FCSTD DOCUMENT  (FreeCAD 0.18R4 (GitTag))
Label: tmp
License: All rights reserved
LicenseURL: http://en.wikipedia.org/wiki/All_rights_reserved
objects: Sketcher::SketchObject×6, PartDesign::Body×2, Spreadsheet::Sheet×1
note: 8 computed .brp shape members not serialized (recipe doc carries the construction recipe); baked Part::Feature solids carry a one-line shape summary decoded from their .brp

FEATURE [Spreadsheet::Sheet] Spreadsheet  label="Variables"
  cells = A2=slotNumber; B2(slotNumber)=12; A3=outerDiameter; B3(outerDiameter)=32; A4=innerDiameter; B4(innerDiameter)=6; A5=stackLength; B5(stackLength)=31; A6=stackingFactor; B6(stackingFactor)=0.95; A7=cuttingThickness; B7(cuttingThickness)=0.1; A8=skewAngle; B8(skewAngle)=14.5; A9=segmentAngle; B9(segmentAngle)==360 / slotNumber; A10=tipHeightReduction; B10(tipHeightReduction)=0; A11=toothThickness; B11(toothThickness)=2.2; A12=yokeThickness; B12(yokeThickness)=5; A13=tipHeight; B13(tipHeight)=1.5; A14=tipAngle; B14(tipAngle)=90; A15=openingLeft; B15(openingLeft)=1; A16=openingRight; B16(openingRight)=1; A17=slotIsolation; B17(slotIsolation)=0.25; A18=windingAngle; B18(windingAngle)=35; A19=heightRatio; B19(heightRatio)=40; A20=roundingRadii; B20(roundingRadii)=0.3; A21=coilAxialHeight; B21(coilAxialHeight)=7.896000000000001
FEATURE [Sketcher::SketchObject] Sketch003  label="StatorSegment"
  MapMode = 5
  Support = -> [XY_Plane]
  expr: Constraints[71] = Variables.innerDiameter / 2
  expr: Constraints[26] = Variables.toothThickness / 2
  expr: Constraints[9] = Variables.segmentAngle
  expr: Constraints[27] = Variables.innerDiameter / 2 + Variables.yokeThickness
  expr: Constraints[35] = Variables.roundingRadii
  expr: Constraints[61] = Variables.tipHeight
  expr: Constraints[23] = Variables.tipAngle
  expr: Constraints[16] = Variables.tipHeight * (1 - Variables.tipHeightReduction / 100)
  expr: Constraints[12] = Variables.openingLeft
  expr: Constraints[72] = Variables.segmentAngle / 2
  expr: Constraints[5] = Variables.outerDiameter
  sketch-geometry (29):
    g0: ArcOfCircle [constr] CenterX=0 CenterY=0 CenterZ=0 NormalX=0 NormalY=0 NormalZ=1 AngleXU=0 Radius=16 StartAngle=0 EndAngle=0.523599
    g1: LineSegment [constr] StartX=0 StartY=0 StartZ=0 EndX=13.8564 EndY=8 EndZ=0
    g2: LineSegment [constr] StartX=0 StartY=0 StartZ=0 EndX=16 EndY=3e-16 EndZ=0
    g3: LineSegment [constr] StartX=0 StartY=0 StartZ=0 EndX=15.4548 EndY=4.1411 EndZ=0
    g4: LineSegment [constr] StartX=11.9984 StartY=10.5848 StartZ=0 EndX=15.1659 EndY=5.09847 EndZ=0
    g5: LineSegment [constr] StartX=15.1659 StartY=5.09847 StartZ=0 EndX=13.9394 EndY=4.76982 EndZ=0
    g6: LineSegment [constr] StartX=13.717 StartY=4.71024 StartZ=0 EndX=15.1659 EndY=5.09847 EndZ=0
    g7: ArcOfCircle CenterX=4.32e-14 CenterY=2.49e-14 CenterZ=0 NormalX=0 NormalY=0 NormalZ=1 AngleXU=0 Radius=16 StartAngle=0.32431 EndAngle=0.523599
    g8: LineSegment StartX=13.6019 StartY=4.9096 StartZ=0 EndX=13.0274 EndY=5.90478 EndZ=0
    g9: LineSegment StartX=12.6176 StartY=6.01459 StartZ=0 EndX=7.66671 EndY=3.1562 EndZ=0
    g10: LineSegment StartX=7.52693 StartY=2.81875 StartZ=0 EndX=7.72741 EndY=2.07055 EndZ=0
    g11: LineSegment [constr] StartX=7.66671 StartY=3.1562 StartZ=0 EndX=7.11671 EndY=4.10883 EndZ=0
    g12: LineSegment StartX=7.72741 StartY=2.07055 StartZ=0 EndX=7.92789 EndY=1.32235 EndZ=0
    g13: LineSegment StartX=8.21766 StartY=1.1 StartZ=0 EndX=13.9344 EndY=1.1 EndZ=0
    g14: LineSegment StartX=14.2344 StartY=1.4 StartZ=0 EndX=14.2344 EndY=2.54914 EndZ=0
    g15: LineSegment StartX=14.4568 StartY=2.83891 StartZ=0 EndX=15.6833 EndY=3.16756 EndZ=0
    g16: ArcOfCircle CenterX=6.7e-15 CenterY=0 CenterZ=0 NormalX=0 NormalY=0 NormalZ=1 AngleXU=0 Radius=16 StartAngle=0 EndAngle=0.199289
    g17: ArcOfCircle CenterX=14.5344 CenterY=2.54914 CenterZ=0 NormalX=0 NormalY=0 NormalZ=1 AngleXU=0 Radius=0.3 StartAngle=1.8326 EndAngle=3.14159
    g18: ArcOfCircle CenterX=13.9344 CenterY=1.4 CenterZ=0 NormalX=0 NormalY=0 NormalZ=1 AngleXU=0 Radius=0.3 StartAngle=4.71239 EndAngle=6.28319
    g19: ArcOfCircle CenterX=8.21766 CenterY=1.4 CenterZ=0 NormalX=0 NormalY=0 NormalZ=1 AngleXU=0 Radius=0.3 StartAngle=3.40339 EndAngle=4.71239
    g20: ArcOfCircle CenterX=12.7676 CenterY=5.75478 CenterZ=0 NormalX=0 NormalY=0 NormalZ=1 AngleXU=0 Radius=0.3 StartAngle=0.523599 EndAngle=2.0944
    g21: ArcOfCircle CenterX=13.8618 CenterY=5.0596 CenterZ=0 NormalX=0 NormalY=0 NormalZ=1 AngleXU=0 Radius=0.3 StartAngle=3.66519 EndAngle=4.97419
    g22: ArcOfCircle CenterX=7.81671 CenterY=2.8964 CenterZ=0 NormalX=0 NormalY=0 NormalZ=1 AngleXU=0 Radius=0.3 StartAngle=2.0944 EndAngle=3.40339
    g23: LineSegment [constr] StartX=13.6019 StartY=4.9096 StartZ=0 EndX=13.717 EndY=4.71024 EndZ=0
    g24: LineSegment [constr] StartX=13.717 StartY=4.71024 StartZ=0 EndX=13.9394 EndY=4.76982 EndZ=0
    g25: LineSegment StartX=13.9394 StartY=4.76982 StartZ=0 EndX=15.1659 EndY=5.09847 EndZ=0
    g26: LineSegment StartX=13.8564 StartY=8 StartZ=0 EndX=2.59808 EndY=1.5 EndZ=0
    g27: LineSegment StartX=3 StartY=1e-16 StartZ=0 EndX=16 EndY=3e-16 EndZ=0
    g28: ArcOfCircle CenterX=0 CenterY=0 CenterZ=0 NormalX=0 NormalY=0 NormalZ=1 AngleXU=0 Radius=3 StartAngle=0 EndAngle=0.523599
  constraints (73):
    c: Coincident(g0,g-1)
    c: Coincident(g1,g0)
    c: Coincident(g1,g0)
    c: Coincident(g2,g0)
    c: Coincident(g2,g0)
    c: Diameter(g0) = 32
    c: Coincident(g3,g0)
    c: PointOnObject(g3,g0)
    c: Symmetric(g0,g0,g3)
    c: Angle(g2,g1) = 0.523599
    c: PointOnObject(g4,g0)
    c: Symmetric(g4,g4,g1)
    c: Distance(g4,g3) = 1
    c: Coincident(g5,g4)
    c: Parallel(g5,g3)
    c: PointOnObject(g6,g5)
    c: Distance(g6) = 1.5
    c: Coincident(g7,g0)
    c: Coincident(g7,g6)
    c: PointOnObject(g7,g1)
    c: PointOnObject(g10,g3)
    c: Perpendicular(g3,g10)
    c: Parallel(g1,g9)
    c: Angle(g9,g8) = 1.5708
    c: PointOnObject(g11,g1)
    c: Perpendicular(g1,g11)
    c: Distance(g11) = 1.1
    c: Distance(g-1,g10) = 8
    c: Coincident(g12,g10)
    c: Symmetric(g15,g7,g3)
    c: PointOnObject(g16,g2)
    c: Coincident(g16,g0)
    c: Coincident(g16,g15)
    c: Tangent(g14,g17) = 1.5708
    c: Tangent(g15,g17) = 1.5708
    c: Radius(g17) = 0.3
    c: Tangent(g13,g18) = -1.5708
    c: Tangent(g14,g18) = -1.5708
    c: Tangent(g12,g19) = -1.5708
    c: Tangent(g13,g19) = -1.5708
    c: Tangent(g8,g20) = -1.5708
    c: Tangent(g9,g20) = -1.5708
    c: Tangent(g5,g21) = 1.5708
    c: Tangent(g8,g21) = 1.5708
    c: Tangent(g10,g22) = -1.5708
    c: Tangent(g9,g22) = -1.5708
    c: Coincident(g11,g9)
    c: Equal(g17,g18)
    c: Equal(g19,g17)
    c: Equal(g22,g17)
    c: Equal(g20,g17)
    c: Symmetric(g13,g9,g3)
    c: Symmetric(g14,g8,g3)
    c: Symmetric(g14,g8,g3)
    c: Equal(g21,g17)
    c: Coincident(g23,g8)
    c: Coincident(g24,g23)
    c: Coincident(g24,g5)
    c: Parallel(g23,g8)
    c: Parallel(g24,g5)
    c: Coincident(g6,g23)
    c: Distance(g6,g4) = 1.5
    c: Coincident(g25,g21)
    c: Coincident(g25,g7)
    c: Coincident(g26,g7)
    c: PointOnObject(g26,g1)
    c: PointOnObject(g27,g2)
    c: Coincident(g27,g16)
    c: Coincident(g28,g-1)
    c: Coincident(g28,g26)
    c: Coincident(g28,g27)
    c: Radius(g28) = 3
    c: Angle(g-1,g3) = 0.261799
FEATURE [Sketcher::SketchObject] Sketch  label="StatorSde"
  MapMode = 5
  Support = -> [XY_Plane001]
  expr: Constraints[20] = Variables.stackLength
  expr: Constraints[17] = Variables.innerDiameter
  expr: Constraints[16] = Variables.outerDiameter
  sketch-geometry (8):
    g0: LineSegment StartX=-15.5 StartY=16 StartZ=0 EndX=15.5 EndY=16 EndZ=0
    g1: LineSegment StartX=15.5 StartY=16 StartZ=0 EndX=15.5 EndY=3 EndZ=0
    g2: LineSegment StartX=15.5 StartY=3 StartZ=0 EndX=-15.5 EndY=3 EndZ=0
    g3: LineSegment StartX=-15.5 StartY=3 StartZ=0 EndX=-15.5 EndY=16 EndZ=0
    g4: LineSegment StartX=-15.5 StartY=-3 StartZ=0 EndX=15.5 EndY=-3 EndZ=0
    g5: LineSegment StartX=15.5 StartY=-3 StartZ=0 EndX=15.5 EndY=-16 EndZ=0
    g6: LineSegment StartX=15.5 StartY=-16 StartZ=0 EndX=-15.5 EndY=-16 EndZ=0
    g7: LineSegment StartX=-15.5 StartY=-16 StartZ=0 EndX=-15.5 EndY=-3 EndZ=0
  constraints (21):
    c: Coincident(g0,g1)
    c: Coincident(g1,g2)
    c: Coincident(g2,g3)
    c: Coincident(g3,g0)
    c: Horizontal(g0)
    c: Vertical(g1)
    c: Vertical(g3)
    c: Coincident(g4,g5)
    c: Coincident(g5,g6)
    c: Coincident(g6,g7)
    c: Coincident(g7,g4)
    c: Horizontal(g6)
    c: Vertical(g5)
    c: Vertical(g7)
    c: Symmetric(g2,g1,g-2)
    c: Symmetric(g4,g4,g-2)
    c: DistanceY(g6,g0) = 32
    c: DistanceY(g4,g2) = 6
    c: Symmetric(g4,g2,g-1)
    c: Equal(g7,g3)
    c: DistanceX(g6,g6) = 31
FEATURE [Sketcher::SketchObject] Sketch009  label="WindingSide"
  ExternalGeometry = -> [Sketch]
  MapMode = 5
  Support = -> [XY_Plane001]
  expr: Constraints[18] = Variables.coilAxialHeight
  expr: Constraints[8] = Variables.coilAxialHeight
  sketch-geometry (12):
    g0: ArcOfEllipse CenterX=-15.5 CenterY=0 CenterZ=0 NormalX=0 NormalY=0 NormalZ=1 MajorRadius=16 MinorRadius=7.896 AngleXU=1.5708 StartAngle=0 EndAngle=3.14159
    g1: LineSegment [constr] StartX=-15.5 StartY=16 StartZ=0 EndX=-15.5 EndY=-16 EndZ=0
    g2: LineSegment [constr] StartX=-23.396 StartY=0 StartZ=0 EndX=-7.604 EndY=0 EndZ=0
    g3: GeomPoint X=-15.5 Y=13.9159 Z=0
    g4: GeomPoint X=-15.5 Y=-13.9159 Z=0
    g5: LineSegment StartX=-15.5 StartY=16 StartZ=0 EndX=-15.5 EndY=-16 EndZ=0
    g6: ArcOfEllipse CenterX=15.5 CenterY=0 CenterZ=0 NormalX=0 NormalY=0 NormalZ=1 MajorRadius=16 MinorRadius=7.896 AngleXU=-1.5708 StartAngle=0 EndAngle=3.14159
    g7: LineSegment [constr] StartX=15.5 StartY=-16 StartZ=0 EndX=15.5 EndY=16 EndZ=0
    g8: LineSegment [constr] StartX=23.396 StartY=0 StartZ=0 EndX=7.604 EndY=0 EndZ=0
    g9: GeomPoint X=15.5 Y=-13.9159 Z=0
    g10: GeomPoint X=15.5 Y=13.9159 Z=0
    g11: LineSegment StartX=15.5 StartY=16 StartZ=0 EndX=15.5 EndY=-16 EndZ=0
  constraints (18):
    c: InternalAlignment(g1-g4 -> g0) x4
    c: PointOnObject(g0,g-4)
    c: Horizontal(g2)
    c: PointOnObject(g0,g-1)
    c: PointOnObject(g1,g-3)
    c: DistanceX(g2,g0) = 7.896
    c: Coincident(g0,g-3)
    c: Coincident(g5,g0)
    c: Coincident(g5,g0)
    c: InternalAlignment(g7-g10 -> g6) x4
    c: PointOnObject(g6,g-1)
    c: Coincident(g6,g-6)
    c: DistanceX(g6,g8) = 7.896
    c: Coincident(g6,g7)
    c: Horizontal(g8)
    c: PointOnObject(g6,g7)
    c: Coincident(g11,g6)
    c: Coincident(g11,g6)
FEATURE [PartDesign::Body] Body001  label="SideView"
  Group = -> [Sketch,Sketch009]
  Origin = -> Origin001
FEATURE [Sketcher::SketchObject] Sketch011  label="Terminal"
  ExternalGeometry = -> [Sketch003]
  MapMode = 5
  Support = -> [XY_Plane]
  expr: Constraints[17] = Variables.innerDiameter / 2 + Variables.yokeThickness + Variables.slotIsolation
  expr: Constraints[31] = Variables.slotIsolation
  expr: Constraints[28] = 90
  expr: Constraints[18] = Variables.toothThickness / 2 + Variables.slotIsolation
  expr: Constraints[2] = (Variables.outerDiameter / 2 - Variables.innerDiameter / 2 - Variables.yokeThickness - Variables.tipHeight) * Variables.heightRatio / 100
  sketch-geometry (12):
    g0: LineSegment [constr] StartX=7.72741 StartY=2.07055 StartZ=0 EndX=10.2388 EndY=2.74348 EndZ=0
    g1: LineSegment StartX=13.3519 StartY=4.84261 StartZ=0 EndX=12.7859 EndY=5.82308 EndZ=0
    g2: LineSegment StartX=12.7859 StartY=5.82308 StartZ=0 EndX=7.75848 EndY=2.92051 EndZ=0
    g3: LineSegment StartX=7.75848 StartY=2.92051 StartZ=0 EndX=8.1793 EndY=1.35 EndZ=0
    g4: LineSegment StartX=8.1793 StartY=1.35 StartZ=0 EndX=13.9844 EndY=1.35 EndZ=0
    g5: LineSegment StartX=13.9844 StartY=1.35 StartZ=0 EndX=13.9844 EndY=2.48215 EndZ=0
    g6: LineSegment StartX=13.9844 StartY=2.48215 StartZ=0 EndX=13.3519 EndY=4.84261 EndZ=0
    g7: GeomPoint X=7.96889 Y=2.13526 Z=0
    g8: LineSegment [constr] StartX=14.2344 StartY=2.54914 StartZ=0 EndX=13.6019 EndY=4.9096 EndZ=0
    g9: LineSegment [constr] StartX=12.7859 StartY=5.82308 StartZ=0 EndX=12.6609 EndY=6.03959 EndZ=0
    g10: LineSegment [constr] StartX=12.7859 StartY=5.82308 StartZ=0 EndX=13.0024 EndY=5.94808 EndZ=0
    g11: LineSegment [constr] StartX=10.1181 StartY=2.71113 StartZ=0 EndX=10.3596 EndY=2.77583 EndZ=0
  constraints (32):
    c: Coincident(g0,g-6)
    c: Perpendicular(g0,g-5)
    c: Distance(g0) = 2.6
    c: Coincident(g1,g2)
    c: Coincident(g2,g3)
    c: Coincident(g3,g4)
    c: Horizontal(g4)
    c: Coincident(g4,g5)
    c: Coincident(g5,g6)
    c: Coincident(g6,g1)
    c: Parallel(g1,g-3)
    c: Parallel(g5,g-8)
    c: Parallel(g6,g3)
    c: Symmetric(g3,g2,g0)
    c: Symmetric(g4,g1,g0)
    c: PointOnObject(g7,g3)
    c: PointOnObject(g7,g0)
    c: Distance(g-1,g7) = 8.25
    c: DistanceY(g-1,g3) = 1.35
    c: Coincident(g8,g-8)
    c: Coincident(g8,g-3)
    c: Equal(g8,g6)
    c: Coincident(g9,g1)
    c: PointOnObject(g9,g-4)
    c: Coincident(g10,g1)
    c: PointOnObject(g10,g-3)
    c: Angle(g10,g9) = 1.5708
    c: Equal(g9,g10)
    c: Angle(g1,g10) = 1.5708
    c: PointOnObject(g11,g0)
    c: Symmetric(g11,g11,g0)
    c: Distance(g11,g11) = 0.25
FEATURE [Sketcher::SketchObject] SlotWindingsIsolation
  MapMode = 5
  Support = -> [XY_Plane]
  sketch-geometry (20):
    g0: Circle CenterX=8.14161 CenterY=2.76182 CenterZ=0 NormalX=0 NormalY=0 NormalZ=1 AngleXU=0 Radius=0.329
    g1: Circle CenterX=8.32113 CenterY=2.09182 CenterZ=0 NormalX=0 NormalY=0 NormalZ=1 AngleXU=0 Radius=0.329
    g2: Circle CenterX=8.8116 CenterY=2.58229 CenterZ=0 NormalX=0 NormalY=0 NormalZ=1 AngleXU=0 Radius=0.329
    g3: Circle CenterX=8.99112 CenterY=1.9123 CenterZ=0 NormalX=0 NormalY=0 NormalZ=1 AngleXU=0 Radius=0.329
    g4: Circle CenterX=9.30207 CenterY=3.07276 CenterZ=0 NormalX=0 NormalY=0 NormalZ=1 AngleXU=0 Radius=0.329
    g5: Circle CenterX=9.48159 CenterY=2.40277 CenterZ=0 NormalX=0 NormalY=0 NormalZ=1 AngleXU=0 Radius=0.329
    g6: Circle CenterX=9.66112 CenterY=1.73278 CenterZ=0 NormalX=0 NormalY=0 NormalZ=1 AngleXU=0 Radius=0.329
    g7: Circle CenterX=9.79254 CenterY=3.56323 CenterZ=0 NormalX=0 NormalY=0 NormalZ=1 AngleXU=0 Radius=0.329
    g8: Circle CenterX=9.97206 CenterY=2.89324 CenterZ=0 NormalX=0 NormalY=0 NormalZ=1 AngleXU=0 Radius=0.329
    g9: Circle CenterX=10.1516 CenterY=2.22325 CenterZ=0 NormalX=0 NormalY=0 NormalZ=1 AngleXU=0 Radius=0.329
    g10: Circle CenterX=10.3311 CenterY=1.55325 CenterZ=0 NormalX=0 NormalY=0 NormalZ=1 AngleXU=0 Radius=0.329
    g11: Circle CenterX=10.283 CenterY=4.0537 CenterZ=0 NormalX=0 NormalY=0 NormalZ=1 AngleXU=0 Radius=0.329
    g12: Circle CenterX=10.4625 CenterY=3.38371 CenterZ=0 NormalX=0 NormalY=0 NormalZ=1 AngleXU=0 Radius=0.329
    g13: Circle CenterX=10.6421 CenterY=2.71371 CenterZ=0 NormalX=0 NormalY=0 NormalZ=1 AngleXU=0 Radius=0.329
    g14: Circle CenterX=10.8216 CenterY=2.04372 CenterZ=0 NormalX=0 NormalY=0 NormalZ=1 AngleXU=0 Radius=0.329
    g15: Circle CenterX=10.953 CenterY=3.87418 CenterZ=0 NormalX=0 NormalY=0 NormalZ=1 AngleXU=0 Radius=0.329
    g16: Circle CenterX=11.1325 CenterY=3.20418 CenterZ=0 NormalX=0 NormalY=0 NormalZ=1 AngleXU=0 Radius=0.329
    g17: Circle CenterX=11.312 CenterY=2.53419 CenterZ=0 NormalX=0 NormalY=0 NormalZ=1 AngleXU=0 Radius=0.329
    g18: Circle CenterX=11.4916 CenterY=1.8642 CenterZ=0 NormalX=0 NormalY=0 NormalZ=1 AngleXU=0 Radius=0.329
    g19: Circle CenterX=11.4435 CenterY=4.36464 CenterZ=0 NormalX=0 NormalY=0 NormalZ=1 AngleXU=0 Radius=0.329
FEATURE [Sketcher::SketchObject] SlotWindingsConductor
  MapMode = 5
  Support = -> [XY_Plane]
  sketch-geometry (20):
    g0: Circle CenterX=8.14161 CenterY=2.76182 CenterZ=0 NormalX=0 NormalY=0 NormalZ=1 AngleXU=0 Radius=0.315
    g1: Circle CenterX=8.32113 CenterY=2.09182 CenterZ=0 NormalX=0 NormalY=0 NormalZ=1 AngleXU=0 Radius=0.315
    g2: Circle CenterX=8.8116 CenterY=2.58229 CenterZ=0 NormalX=0 NormalY=0 NormalZ=1 AngleXU=0 Radius=0.315
    g3: Circle CenterX=8.99112 CenterY=1.9123 CenterZ=0 NormalX=0 NormalY=0 NormalZ=1 AngleXU=0 Radius=0.315
    g4: Circle CenterX=9.30207 CenterY=3.07276 CenterZ=0 NormalX=0 NormalY=0 NormalZ=1 AngleXU=0 Radius=0.315
    g5: Circle CenterX=9.48159 CenterY=2.40277 CenterZ=0 NormalX=0 NormalY=0 NormalZ=1 AngleXU=0 Radius=0.315
    g6: Circle CenterX=9.66112 CenterY=1.73278 CenterZ=0 NormalX=0 NormalY=0 NormalZ=1 AngleXU=0 Radius=0.315
    g7: Circle CenterX=9.79254 CenterY=3.56323 CenterZ=0 NormalX=0 NormalY=0 NormalZ=1 AngleXU=0 Radius=0.315
    g8: Circle CenterX=9.97206 CenterY=2.89324 CenterZ=0 NormalX=0 NormalY=0 NormalZ=1 AngleXU=0 Radius=0.315
    g9: Circle CenterX=10.1516 CenterY=2.22325 CenterZ=0 NormalX=0 NormalY=0 NormalZ=1 AngleXU=0 Radius=0.315
    g10: Circle CenterX=10.3311 CenterY=1.55325 CenterZ=0 NormalX=0 NormalY=0 NormalZ=1 AngleXU=0 Radius=0.315
    g11: Circle CenterX=10.283 CenterY=4.0537 CenterZ=0 NormalX=0 NormalY=0 NormalZ=1 AngleXU=0 Radius=0.315
    g12: Circle CenterX=10.4625 CenterY=3.38371 CenterZ=0 NormalX=0 NormalY=0 NormalZ=1 AngleXU=0 Radius=0.315
    g13: Circle CenterX=10.6421 CenterY=2.71371 CenterZ=0 NormalX=0 NormalY=0 NormalZ=1 AngleXU=0 Radius=0.315
    g14: Circle CenterX=10.8216 CenterY=2.04372 CenterZ=0 NormalX=0 NormalY=0 NormalZ=1 AngleXU=0 Radius=0.315
    g15: Circle CenterX=10.953 CenterY=3.87418 CenterZ=0 NormalX=0 NormalY=0 NormalZ=1 AngleXU=0 Radius=0.315
    g16: Circle CenterX=11.1325 CenterY=3.20418 CenterZ=0 NormalX=0 NormalY=0 NormalZ=1 AngleXU=0 Radius=0.315
    g17: Circle CenterX=11.312 CenterY=2.53419 CenterZ=0 NormalX=0 NormalY=0 NormalZ=1 AngleXU=0 Radius=0.315
    g18: Circle CenterX=11.4916 CenterY=1.8642 CenterZ=0 NormalX=0 NormalY=0 NormalZ=1 AngleXU=0 Radius=0.315
    g19: Circle CenterX=11.4435 CenterY=4.36464 CenterZ=0 NormalX=0 NormalY=0 NormalZ=1 AngleXU=0 Radius=0.315
FEATURE [PartDesign::Body] Body  label="TopView"
  Group = -> [Sketch003,Sketch011,SlotWindingsIsolation,SlotWindingsConductor]
  Origin = -> Origin
